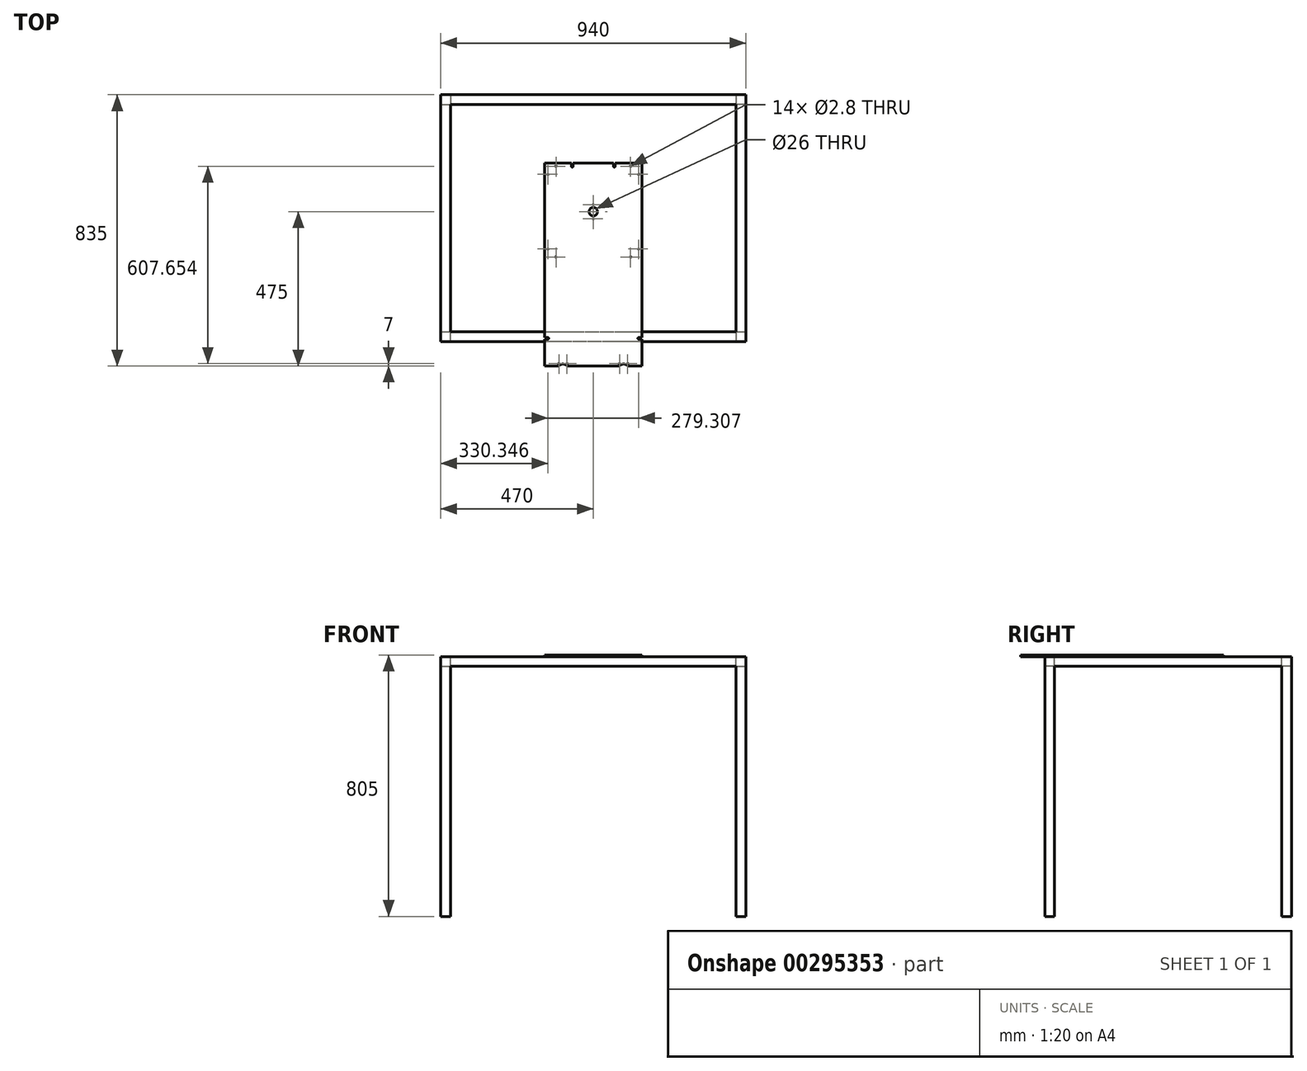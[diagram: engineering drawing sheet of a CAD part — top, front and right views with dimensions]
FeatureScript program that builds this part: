
annotation { "Feature Type Name" : "Feature", "Feature Type Description" : "" }
export const myFeature = defineFeature(function(context is Context, id is Id, definition is map)
    precondition{}
    {
        {
            var Q0;
            Q0=qCreatedBy(makeId("Top.planeOp"),FACE);
            var sketch = newSketch(context, id + "F0", { "sketchPlane" : qUnion([Q0])});
            skLineSegment(sketch, "E0.bottom", {"start": v(-150, 150) * mm, "end": v(-67.5, 150) * mm});
            skCircle(sketch, "E1", {"center": v(0, 0) * mm, "radius": 13 * mm});
            skCircle(sketch, "E2.1.0", {"center": v(-139.65, 114.9) * mm, "radius": 1.4 * mm});
            skCircle(sketch, "E2.1.1", {"center": v(-114.9, 139.65) * mm, "radius": 1.4 * mm});
            skCircle(sketch, "E2.3.0", {"center": v(-114.9, -139.65) * mm, "radius": 1.4 * mm});
            skCircle(sketch, "E2.3.1", {"center": v(-139.65, -114.9) * mm, "radius": 1.4 * mm});
            skCircle(sketch, "E2.5.0", {"center": v(139.65, -114.9) * mm, "radius": 1.4 * mm});
            skCircle(sketch, "E2.5.1", {"center": v(114.9, -139.65) * mm, "radius": 1.4 * mm});
            skCircle(sketch, "E2.7.0", {"center": v(114.9, 139.65) * mm, "radius": 1.4 * mm});
            skCircle(sketch, "E2.7.1", {"center": v(139.65, 114.9) * mm, "radius": 1.4 * mm});
            skArc(sketch, "E3", {"start": v(-140, -392.5) * mm, "mid": v(-137.5, -390) * mm, "end": v(-140, -387.5) * mm});
            skArc(sketch, "E4", {"start": v(-67.5, 140) * mm, "mid": v(-65, 137.5) * mm, "end": v(-62.5, 140) * mm});
            skCircle(sketch, "E5", {"center": v(0, -22) * mm, "radius": 1.4 * mm});
            skCircle(sketch, "E6.MirrorC", {"center": v(0, 22) * mm, "radius": 1.4 * mm});
            skCircle(sketch, "E7", {"center": v(-106, -468) * mm, "radius": 1.4 * mm});
            skCircle(sketch, "E8", {"center": v(-81, -468) * mm, "radius": 1.4 * mm});
            skLineSegment(sketch, "E9", {"start": v(-150, 150) * mm, "end": v(-150, -387.5) * mm});
            skLineSegment(sketch, "E10", {"start": v(150, -475) * mm, "end": v(150, -392.5) * mm});
            skLineSegment(sketch, "E11", {"start": v(-140, -392.5) * mm, "end": v(-150, -392.5) * mm});
            skLineSegment(sketch, "E12", {"start": v(-140, -387.5) * mm, "end": v(-150, -387.5) * mm});
            skLineSegment(sketch, "E13", {"start": v(-67.5, 140) * mm, "end": v(-67.5, 150) * mm});
            skLineSegment(sketch, "E14", {"start": v(-62.5, 140) * mm, "end": v(-62.5, 150) * mm});
            skLineSegment(sketch, "E15.trimOffspring", {"start": v(-150, -392.5) * mm, "end": v(-150, -475) * mm});
            skLineSegment(sketch, "E16.trimOffspring", {"start": v(-62.5, 150) * mm, "end": v(62.5, 150) * mm});
            skLineSegment(sketch, "E17.MirrorCS", {"start": v(140, -392.5) * mm, "end": v(150, -392.5) * mm});
            skLineSegment(sketch, "E18.MirrorCS", {"start": v(140, -387.5) * mm, "end": v(150, -387.5) * mm});
            skLineSegment(sketch, "E19.MirrorCS", {"start": v(67.5, 140) * mm, "end": v(67.5, 150) * mm});
            skLineSegment(sketch, "E20.MirrorCS", {"start": v(62.5, 140) * mm, "end": v(62.5, 150) * mm});
            skLineSegment(sketch, "E21.trimOffspring", {"start": v(67.5, 150) * mm, "end": v(150, 150) * mm});
            skLineSegment(sketch, "E22.trimOffspring", {"start": v(150, -387.5) * mm, "end": v(150, 150) * mm});
            skArc(sketch, "E23", {"start": v(-81, -475) * mm, "mid": v(-93.5, -469) * mm, "end": v(-106, -475) * mm});
            skLineSegment(sketch, "E24.trimOffspring", {"start": v(-106, -475) * mm, "end": v(-150, -475) * mm});
            skLineSegment(sketch, "E25", {"start": v(0, -475) * mm, "end": v(-81, -475) * mm});
            skLineSegment(sketch, "E26.MirrorCS", {"start": v(106, -475) * mm, "end": v(150, -475) * mm});
            skLineSegment(sketch, "E27.MirrorCS", {"start": v(0, -475) * mm, "end": v(81, -475) * mm});
            skArc(sketch, "E28", {"start": v(62.5, 140) * mm, "mid": v(65, 137.5) * mm, "end": v(67.5, 140) * mm});
            skArc(sketch, "E29", {"start": v(140, -387.5) * mm, "mid": v(137.5, -390) * mm, "end": v(140, -392.5) * mm});
            skArc(sketch, "E30", {"start": v(106, -475) * mm, "mid": v(93.5, -469) * mm, "end": v(81, -475) * mm});
            skCircle(sketch, "E31", {"center": v(81, -468) * mm, "radius": 1.4 * mm});
            skCircle(sketch, "E32", {"center": v(106, -468) * mm, "radius": 1.4 * mm});
            skSolve(sketch);
        }
        {
            var Q0;
            Q0=qCreatedBy(makeId("Top.planeOp"),FACE);
            var sketch = newSketch(context, id + "F1", { "sketchPlane" : qUnion([Q0])});
            skLineSegment(sketch, "E33.top", {"start": v(-470, 360) * mm, "end": v(470, 360) * mm});
            skLineSegment(sketch, "E34.top", {"start": v(470, -400) * mm, "end": v(-470, -400) * mm});
            skLineSegment(sketch, "E34.left", {"start": v(470, 360) * mm, "end": v(470, -400) * mm});
            skLineSegment(sketch, "E34.right", {"start": v(-470, 360) * mm, "end": v(-470, -400) * mm});
            skLineSegment(sketch, "E35.bottom", {"start": v(-440, 330) * mm, "end": v(440, 330) * mm});
            skLineSegment(sketch, "E35.top", {"start": v(-440, -370) * mm, "end": v(440, -370) * mm});
            skLineSegment(sketch, "E35.left", {"start": v(-440, 330) * mm, "end": v(-440, -370) * mm});
            skLineSegment(sketch, "E35.right", {"start": v(440, 330) * mm, "end": v(440, -370) * mm});
            skPoint(sketch, "E36", {"position": v(0, 0) * mm});
            skLineSegment(sketch, "E37.bottom", {"start": v(50, 330) * mm, "end": v(80, 330) * mm});
            skLineSegment(sketch, "E37.top", {"start": v(50, -370) * mm, "end": v(80, -370) * mm});
            skLineSegment(sketch, "E37.left", {"start": v(50, 330) * mm, "end": v(50, -370) * mm});
            skLineSegment(sketch, "E37.right", {"start": v(80, 330) * mm, "end": v(80, -370) * mm});
            skLineSegment(sketch, "E38.MirrorCS", {"start": v(-50, 330) * mm, "end": v(-80, 330) * mm});
            skLineSegment(sketch, "E39.MirrorCS", {"start": v(-50, -370) * mm, "end": v(-80, -370) * mm});
            skLineSegment(sketch, "E40.MirrorCS", {"start": v(-50, 330) * mm, "end": v(-50, -370) * mm});
            skLineSegment(sketch, "E41.MirrorCS", {"start": v(-80, 330) * mm, "end": v(-80, -370) * mm});
            skSolve(sketch);
        }
        {
            var Q0;
            Q0=qSketchRegion(id+"F1",true);
            var Q1;
            Q1=makeQuery(id+"F1.imprint","IMPRINT",FACE,{"disambiguationData":[TD([[makeQuery(id+"F1.imprint","IMPRINT",EDGE,{"derivedFrom":sQuery(id+"F1.wireOp",EDGE,"E38.MirrorCS")}),1.0]])]});
            var Q2;
            Q2=makeQuery(id+"F1.imprint","IMPRINT",FACE,{"disambiguationData":[TD([[makeQuery(id+"F1.imprint","IMPRINT",EDGE,{"derivedFrom":sQuery(id+"F1.wireOp",EDGE,"E37.bottom")}),-1.0]])]});
            extrude(context, id + "F2", {"entities" : qUnion([Q0, Q1, Q2]), "oppositeDirection" : true, "depth" : 30 * mm});
        }
        {
            var Q0;
            Q0=qSketchRegion(id+"F0",true);
            extrude(context, id + "F3", {"entities" : qUnion([Q0]), "operationType" : NewBodyOperationType.ADD, "depth" : 5 * mm});
        }
        {
            var Q0;
            Q0=makeQuery(id+"F2.opExtrude","CAP_FACE",FACE,{"disambiguationData":[OSD([sQuery(id+"F1.wireOp",EDGE,"E33.top"),sQuery(id+"F1.wireOp",EDGE,"E34.top"),sQuery(id+"F1.wireOp",EDGE,"E34.left"),sQuery(id+"F1.wireOp",EDGE,"E34.right"),sQuery(id+"F1.wireOp",EDGE,"E35.bottom"),sQuery(id+"F1.wireOp",EDGE,"E35.top"),sQuery(id+"F1.wireOp",EDGE,"E35.left"),sQuery(id+"F1.wireOp",EDGE,"E35.right")])],"isStart":false});
            var sketch = newSketch(context, id + "F4", { "sketchPlane" : qUnion([Q0])});
            skLineSegment(sketch, "E42.bottom", {"start": v(-470, 400) * mm, "end": v(-440, 400) * mm});
            skLineSegment(sketch, "E42.top", {"start": v(-470, 370) * mm, "end": v(-440, 370) * mm});
            skLineSegment(sketch, "E42.left", {"start": v(-470, 400) * mm, "end": v(-470, 370) * mm});
            skLineSegment(sketch, "E42.right", {"start": v(-440, 400) * mm, "end": v(-440, 370) * mm});
            skLineSegment(sketch, "E43.bottom", {"start": v(-470, -360) * mm, "end": v(-440, -360) * mm});
            skLineSegment(sketch, "E43.top", {"start": v(-470, -330) * mm, "end": v(-440, -330) * mm});
            skLineSegment(sketch, "E43.left", {"start": v(-470, -360) * mm, "end": v(-470, -330) * mm});
            skLineSegment(sketch, "E43.right", {"start": v(-440, -360) * mm, "end": v(-440, -330) * mm});
            skLineSegment(sketch, "E44.bottom", {"start": v(470, -360) * mm, "end": v(440, -360) * mm});
            skLineSegment(sketch, "E44.top", {"start": v(470, -330) * mm, "end": v(440, -330) * mm});
            skLineSegment(sketch, "E44.left", {"start": v(470, -360) * mm, "end": v(470, -330) * mm});
            skLineSegment(sketch, "E44.right", {"start": v(440, -360) * mm, "end": v(440, -330) * mm});
            skLineSegment(sketch, "E45.bottom", {"start": v(440, 370) * mm, "end": v(470, 370) * mm});
            skLineSegment(sketch, "E45.top", {"start": v(440, 400) * mm, "end": v(470, 400) * mm});
            skLineSegment(sketch, "E45.left", {"start": v(440, 370) * mm, "end": v(440, 400) * mm});
            skLineSegment(sketch, "E45.right", {"start": v(470, 370) * mm, "end": v(470, 400) * mm});
            skSolve(sketch);
        }
        {
            var Q0;
            Q0=qSketchRegion(id+"F4",true);
            extrude(context, id + "F5", {"entities" : qUnion([Q0]), "operationType" : NewBodyOperationType.ADD, "depth" : 770 * mm});
        }
    });
